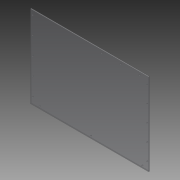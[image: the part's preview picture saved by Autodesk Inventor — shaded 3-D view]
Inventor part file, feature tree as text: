
AUTODESK INVENTOR PART (.ipt)
format: ipt  version: 2014 SP1 (Build 180222100, 222)  size: 103,424 bytes
history: native  units: in
note: dims shown in document units (in); Inventor stores cm internally (conversion verified against a paired STEP export)
features: reference x3, extrude x1, sketch x1
ambient origin geometry x8: Origin, YZ Plane, XZ Plane, XY Plane, X Axis, Y Axis, Z Axis, Center Point
bodies: Solid1 (feature_tree)
feature tree (5):
  extrude  "Extrusion1"  Depth=13.0in
  sketch  "Sketch1"  dims[d0=18.6938in d1=13.0in d2=0.125in d3=0.0in d4=0.125in d5=1.1811in d7=4.0in d8=0.3937in d10=1.0in d12=0.5in d13=2.0in]
  reference  "Reference1"
  reference  "Reference2"
  reference  "Reference3"
